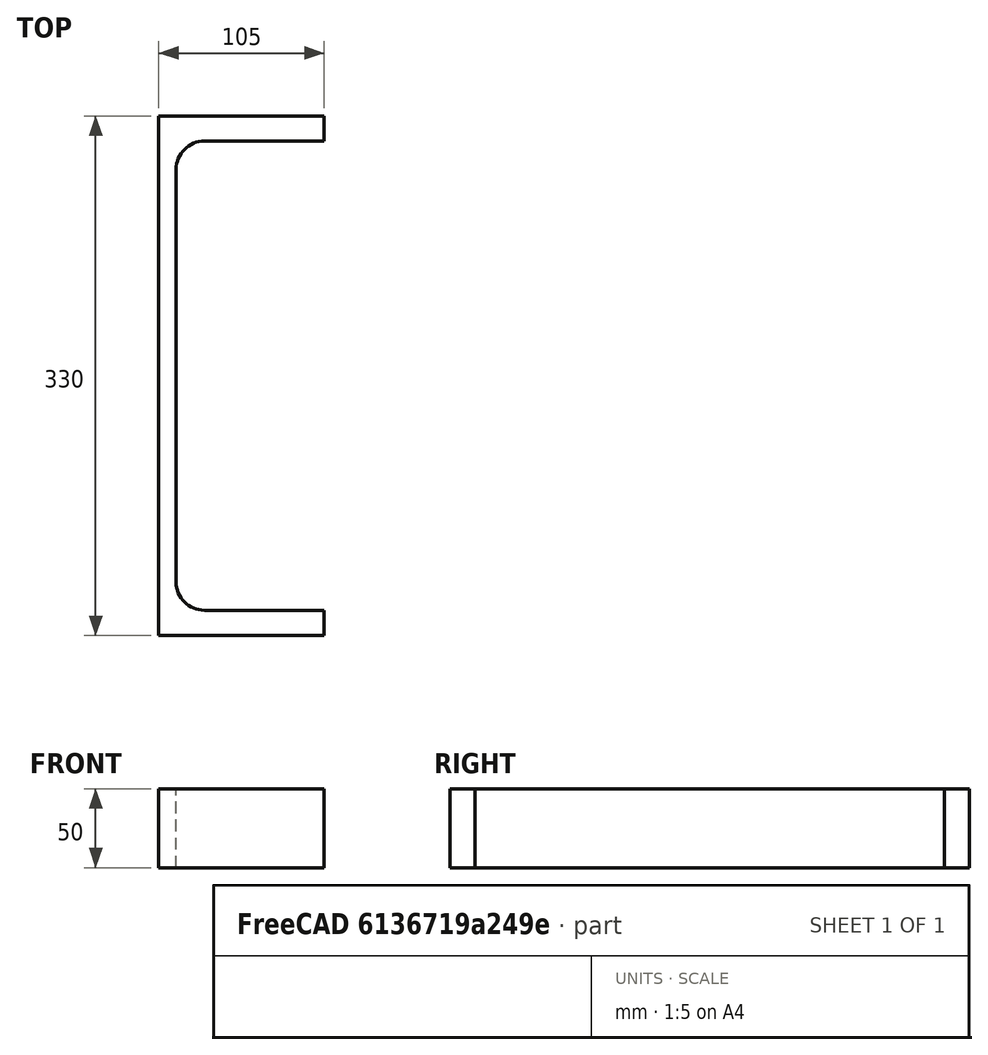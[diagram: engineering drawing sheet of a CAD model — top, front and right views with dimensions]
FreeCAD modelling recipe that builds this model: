
FCSTD DOCUMENT  (FreeCAD 0.20R29410 (Git))
Label: UPE-Profile 330 DIN1026-2 S235JR
License: All rights reserved
LicenseURL: http://en.wikipedia.org/wiki/All_rights_reserved
objects: Sketcher::SketchObject×1, Part::Extrusion×1
note: 2 computed .brp shape members not serialized (recipe doc carries the construction recipe); baked Part::Feature solids carry a one-line shape summary decoded from their .brp

FEATURE [Sketcher::SketchObject] Sketch
  FullyConstrained = true
  MapMode = 5
  sketch-geometry (10):
    g0: LineSegment StartX=11 StartY=-131 StartZ=0 EndX=11 EndY=131 EndZ=0
    g1: LineSegment StartX=29 StartY=149 StartZ=0 EndX=105 EndY=149 EndZ=0
    g2: LineSegment StartX=105 StartY=149 StartZ=0 EndX=105 EndY=165 EndZ=0
    g3: LineSegment StartX=105 StartY=-165 StartZ=0 EndX=105 EndY=-149 EndZ=0
    g4: LineSegment StartX=105 StartY=-149 StartZ=0 EndX=29 EndY=-149 EndZ=0
    g5: ArcOfCircle CenterX=29 CenterY=131 CenterZ=0 NormalX=0 NormalY=0 NormalZ=1 AngleXU=0 Radius=18 StartAngle=1.5708 EndAngle=3.14159
    g6: ArcOfCircle CenterX=29 CenterY=-131 CenterZ=0 NormalX=0 NormalY=0 NormalZ=1 AngleXU=0 Radius=18 StartAngle=3.14159 EndAngle=4.71239
    g7: LineSegment StartX=105 StartY=-165 StartZ=0 EndX=0 EndY=-165 EndZ=0
    g8: LineSegment StartX=0 StartY=-165 StartZ=0 EndX=0 EndY=165 EndZ=0
    g9: LineSegment StartX=0 StartY=165 StartZ=0 EndX=105 EndY=165 EndZ=0
  constraints (27):
    c: Vertical(g0)
    c: Coincident(g2,g1)
    c: Vertical(g2)
    c: Vertical(g3)
    c: Coincident(g4,g3)
    c: Horizontal(g4)
    c: Tangent(g1,g5) = 1.5708
    c: Tangent(g0,g5) = 1.5708
    c: Tangent(g0,g6) = 1.5708
    c: Tangent(g4,g6) = 1.5708
    c: Symmetric(g2,g3,g-1)
    c: DistanceY(g2) = 16
    c: Radius(g5) = 18
    c: Coincident(g3,g7)
    c: PointOnObject(g7,g-2)
    c: Horizontal(g7)
    c: Coincident(g7,g8)
    c: PointOnObject(g8,g-2)
    c: Coincident(g8,g9)
    c: Coincident(g9,g2)
    c: Horizontal(g9)
    c: Distance(g-1,g0) = 11
    c: DistanceX(g9,g9) = 105
    c: Horizontal(g1)
    c: Equal(g3,g2)
    c: Equal(g5,g6)
    c: DistanceY(g3,g2) = 330
FEATURE [Part::Extrusion] Extrude  label="UPE-Profile 330 DIN1026-2 S235JR"
  Base = -> Sketch
  Dir = (0,0,50)
  DirMode = 0
  FaceMakerClass = Part::FaceMakerExtrusion
  LengthFwd = 0
  LengthRev = 0
  Solid = true
  Symmetric = false
